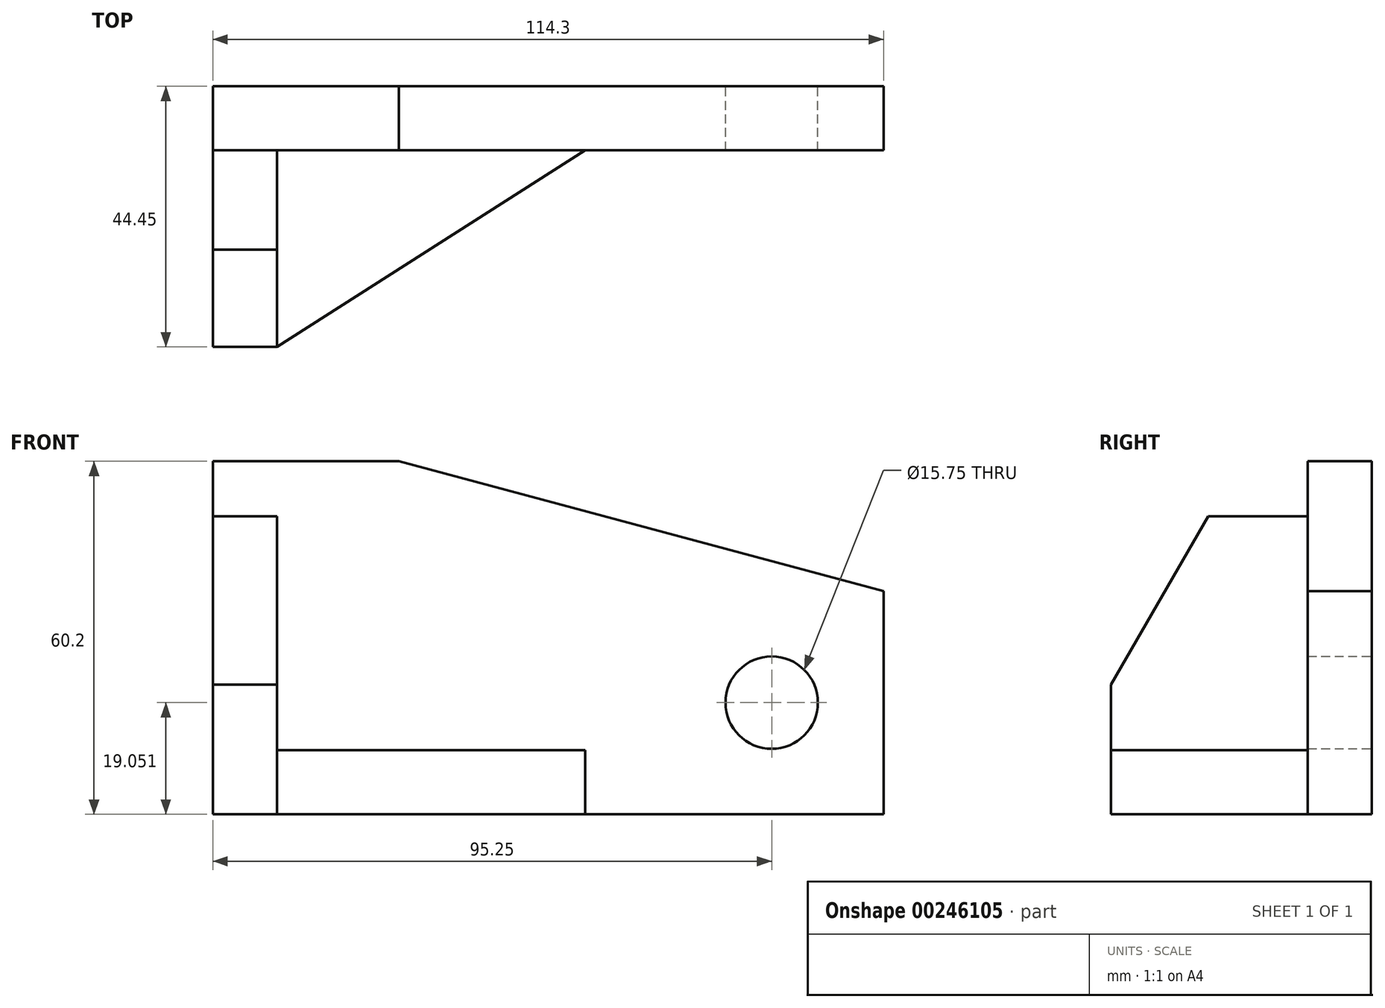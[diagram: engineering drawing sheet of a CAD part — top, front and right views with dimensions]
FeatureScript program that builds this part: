
annotation { "Feature Type Name" : "Feature", "Feature Type Description" : "" }
export const myFeature = defineFeature(function(context is Context, id is Id, definition is map)
    precondition{}
    {
        {
            var Q0;
            Q0=qCreatedBy(makeId("Front.planeOp"),FACE);
            var sketch = newSketch(context, id + "F0", { "sketchPlane" : qUnion([Q0])});
            skLineSegment(sketch, "E0.bottom", {"start": v(-63.5, 22.12) * mm, "end": v(-31.75, 22.12) * mm});
            skLineSegment(sketch, "E0.top", {"start": v(-63.5, -38.08) * mm, "end": v(50.8, -38.08) * mm});
            skLineSegment(sketch, "E0.left", {"start": v(-63.5, 22.12) * mm, "end": v(-63.5, -38.08) * mm});
            skLineSegment(sketch, "E0.right", {"start": v(50.8, 0) * mm, "end": v(50.8, -38.08) * mm});
            skLineSegment(sketch, "E1", {"start": v(-31.75, 22.12) * mm, "end": v(50.8, 0) * mm});
            skLineSegment(sketch, "E2", {"start": v(-52.58, -38.08) * mm, "end": v(-52.58, -15.98) * mm});
            skLineSegment(sketch, "E3", {"start": v(-63.5, -15.98) * mm, "end": v(-52.58, -15.98) * mm});
            skCircle(sketch, "E4", {"center": v(31.75, -19.03) * mm, "radius": 7.87 * mm});
            skLineSegment(sketch, "E5", {"start": v(0, -38.08) * mm, "end": v(0, -27.16) * mm});
            skLineSegment(sketch, "E6", {"start": v(0, -27.16) * mm, "end": v(-52.58, -27.16) * mm});
            skLineSegment(sketch, "E7", {"start": v(-63.5, 12.72) * mm, "end": v(-52.58, 12.72) * mm});
            skLineSegment(sketch, "E8", {"start": v(-52.58, 12.72) * mm, "end": v(-52.58, -15.98) * mm});
            skSolve(sketch);
        }
        {
            var Q0;
            Q0 = qSketchRegion(id + "F0", true);
            extrude(context, id + "F1", {"entities" : qUnion([Q0]), "depth" : 10.92 * mm});
        }
        {
            var Q0;
            {var subQ0=sQuery(id+"F0.wireOp",EDGE,"E3");Q0=makeQuery(id+"F0.imprint","IMPRINT",FACE,{"disambiguationData":[TD([[makeQuery(id+"F0.imprint","IMPRINT",EDGE,{"derivedFrom":subQ0}),1.0]])]});}
            var Q1;
            {var subQ0=sQuery(id+"F0.wireOp",EDGE,"E3");Q1=makeQuery(id+"F0.imprint","IMPRINT",FACE,{"disambiguationData":[TD([[makeQuery(id+"F0.imprint","IMPRINT",EDGE,{"derivedFrom":subQ0}),-1.0]])]});}
            var Q2;
            {var subQ3=sQuery(id+"F0.wireOp",EDGE,"E5");Q2=makeQuery(id+"F0.imprint","IMPRINT",FACE,{"disambiguationData":[TD([[makeQuery(id+"F0.imprint","IMPRINT",EDGE,{"derivedFrom":subQ3}),1.0]])]});}
            extrude(context, id + "F2", {"entities" : qUnion([Q0, Q1, Q2]), "operationType" : NewBodyOperationType.ADD, "depth" : 44.45 * mm});
        }
        {
            var Q0;
            Q0=makeQuery(id+"F2.opExtrude","SWEPT_FACE",FACE,{"disambiguationData":[OSD([sQuery(id+"F0.wireOp",EDGE,"E2"),sQuery(id+"F0.wireOp",EDGE,"E8")])]});
            var sketch = newSketch(context, id + "F3", { "sketchPlane" : qUnion([Q0])});
            skLineSegment(sketch, "E9.bottom", {"start": v(-44.45, -27.16) * mm, "end": v(-10.92, -27.16) * mm});
            skLineSegment(sketch, "E9.top", {"start": v(-44.45, 12.72) * mm, "end": v(-10.92, 12.72) * mm});
            skLineSegment(sketch, "E9.left", {"start": v(-44.45, -27.16) * mm, "end": v(-44.45, 12.72) * mm});
            skLineSegment(sketch, "E9.right", {"start": v(-10.92, -27.16) * mm, "end": v(-10.92, 12.72) * mm});
            skLineSegment(sketch, "E10", {"start": v(-44.45, -15.98) * mm, "end": v(-27.88, 12.72) * mm});
            skSolve(sketch);
        }
        {
            var Q0;
            {var subQ3=sQuery(id+"F3.wireOp",EDGE,"E10");Q0=makeQuery(id+"F3.imprint","IMPRINT",FACE,{"disambiguationData":[TD([[makeQuery(id+"F3.imprint","IMPRINT",EDGE,{"derivedFrom":subQ3}),1.0]])]});}
            extrude(context, id + "F4", {"entities" : qUnion([Q0]), "operationType" : NewBodyOperationType.REMOVE, "oppositeDirection" : true, "depth" : 25.4 * mm});
        }
        {
            var Q0;
            Q0=makeQuery(id+"F2.opExtrude","SWEPT_FACE",FACE,{"disambiguationData":[OSD([sQuery(id+"F0.wireOp",EDGE,"E6")])]});
            var sketch = newSketch(context, id + "F5", { "sketchPlane" : qUnion([Q0])});
            skLineSegment(sketch, "E11", {"start": v(-52.58, -44.45) * mm, "end": v(0, -10.92) * mm});
            skSolve(sketch);
        }
        {
            var Q0;
            Q0=makeQuery(id+"F5.imprint","IMPRINT",FACE,{"disambiguationData":[TD([[makeQuery(id+"F5.imprint","IMPRINT",EDGE,{"derivedFrom":sQuery(id+"F5.wireOp",EDGE,"E11")}),-1.0]])]});
            extrude(context, id + "F6", {"entities" : qUnion([Q0]), "operationType" : NewBodyOperationType.REMOVE, "oppositeDirection" : true, "depth" : 25.4 * mm});
        }
    });
